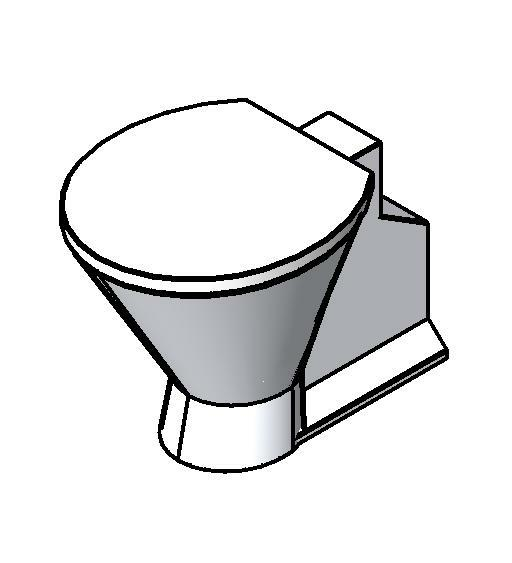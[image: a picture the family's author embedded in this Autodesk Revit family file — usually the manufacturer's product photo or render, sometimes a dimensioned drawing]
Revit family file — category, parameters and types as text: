
# Revit family: Deca_Cuba Semiencaixe quadrada com mesa 50cm _Cuba Slim_L.63050.M
name_source: partatom
category: Plumbing Fixtures
units: mm (PartAtom-declared; Revit-internal decimal feet)

## family parameters
Cut with Voids When Loaded = No
Host = Face
Part Type = Normal
Room Calculation Point = No
Round Connector Dimension = Use Radius
Shared = No

## types (1)
- L.63050.M.17_Branco
    Acompanha o Produto = Acabamento da válvula cerâmica/Smartblock
    Aprovado por = quattroD
    Atendimento ao Cliente = 0800-0117073
    CWFU = 0
    Categoria = CUBAS
    Composição Básica = Composição Básica: Argila / Feldispato / Caulim / Vidrados e corantes inorgânicos / Plásticos de Engenharia.
    Composição Componente = PEBD
    Cor Interna = Branco
    Cor Principal = Branco
    Cores Componente = transparente
    Criado por = quattroD
    Código Pai = L.63050.M.17
    Default Elevation = 0 m
    Diâmetro Ponto de Esgoto = 0 m
    Diâmetro Água Fria = 0 m
    Informações Complementares = Esmalte Protekto
    Linha = CUBA SLIM
    Manufacturer = DECA
    Material = Deca_Branco
    Model = L.63050.M.17
    Norma = NBR 16728-1 / NBR 16728-2
    Peso Líquido (Kg) = 12.3
    Pressão máx. funcionamento = 40mca
    Pressão mín. funcionamento = 3mca
    Raio Ponto de Esgoto = 0 m
    Raio Água Fria = 0 m
    Saída de Esgoto = válvula curta
    Segmento = LUXO
    URL = www.deca.com.br
    WFU = 0

## geometry (parser evidence)
native form markers: Sweep x2
no freeform markers — native parametric forms only
